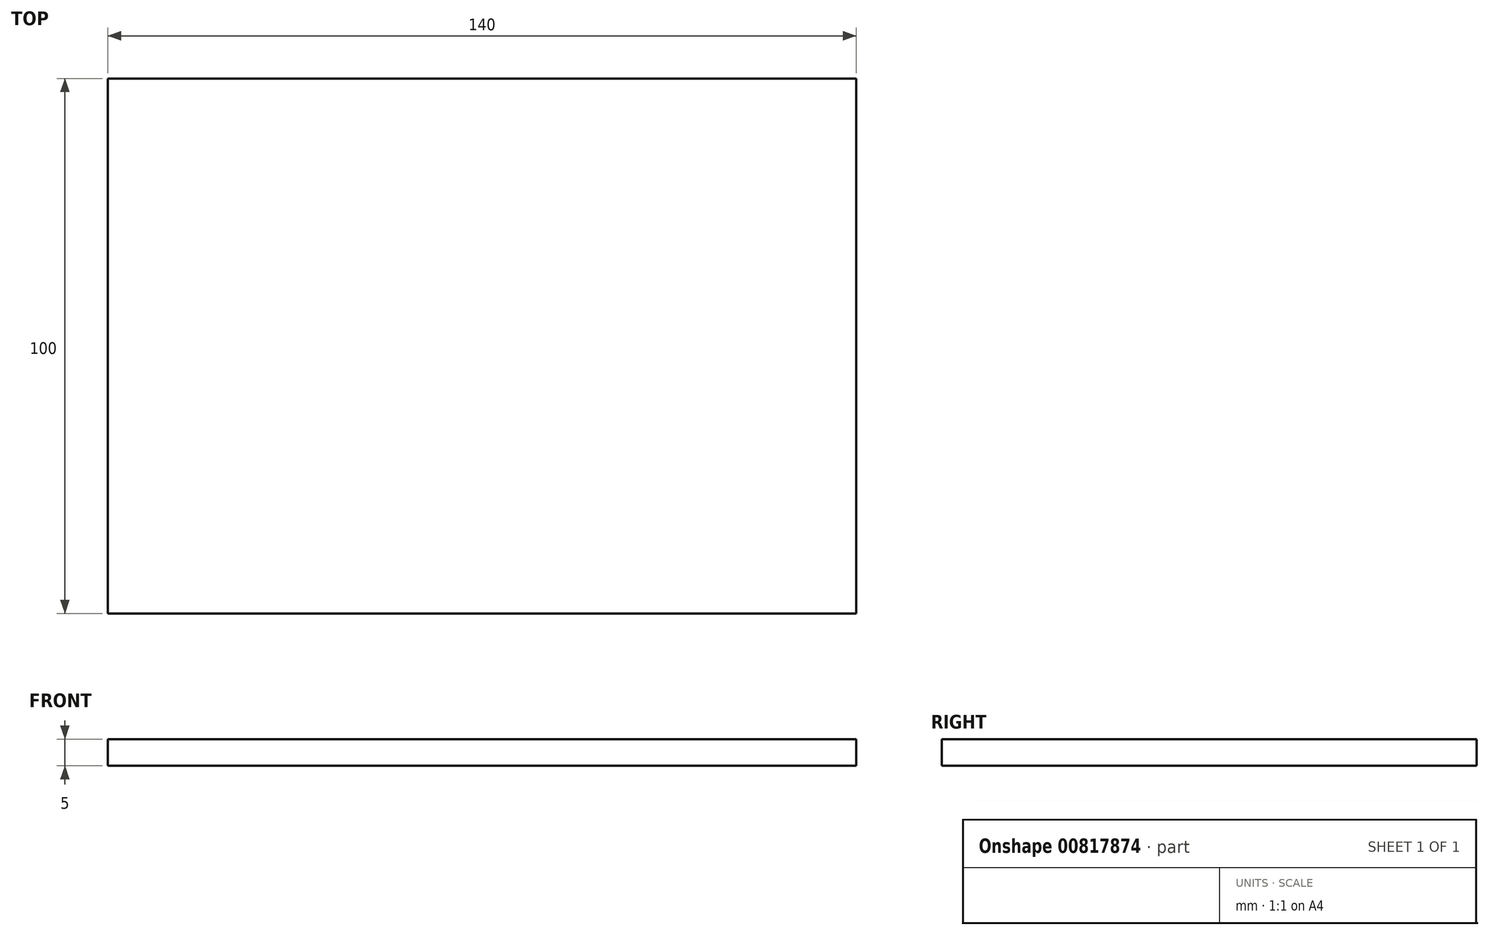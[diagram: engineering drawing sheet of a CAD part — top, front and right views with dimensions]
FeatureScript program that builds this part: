
annotation { "Feature Type Name" : "Feature", "Feature Type Description" : "" }
export const myFeature = defineFeature(function(context is Context, id is Id, definition is map)
    precondition{}
    {
        {
            var Q0;
            Q0=qCreatedBy(makeId("Top.planeOp"),FACE);
            var sketch = newSketch(context, id + "F0", { "sketchPlane" : qUnion([Q0])});
            skLineSegment(sketch, "E0.bottom", {"start": v(0, 0) * mm, "end": v(140, 0) * mm});
            skLineSegment(sketch, "E0.top", {"start": v(0, 100) * mm, "end": v(140, 100) * mm});
            skLineSegment(sketch, "E0.left", {"start": v(0, 0) * mm, "end": v(0, 100) * mm});
            skLineSegment(sketch, "E0.right", {"start": v(140, 0) * mm, "end": v(140, 100) * mm});
            skSolve(sketch);
        }
        {
            var Q0;
            Q0=makeQuery(id+"F0.imprint","IMPRINT",FACE,{"disambiguationData":[TD([[makeQuery(id+"F0.imprint","IMPRINT",EDGE,{"derivedFrom":sQuery(id+"F0.wireOp",EDGE,"E0.bottom")}),1.0]])]});
            extrude(context, id + "F1", {"entities" : qUnion([Q0]), "depth" : 5 * mm, "offsetDistance" : 25 * mm});
        }
    });
